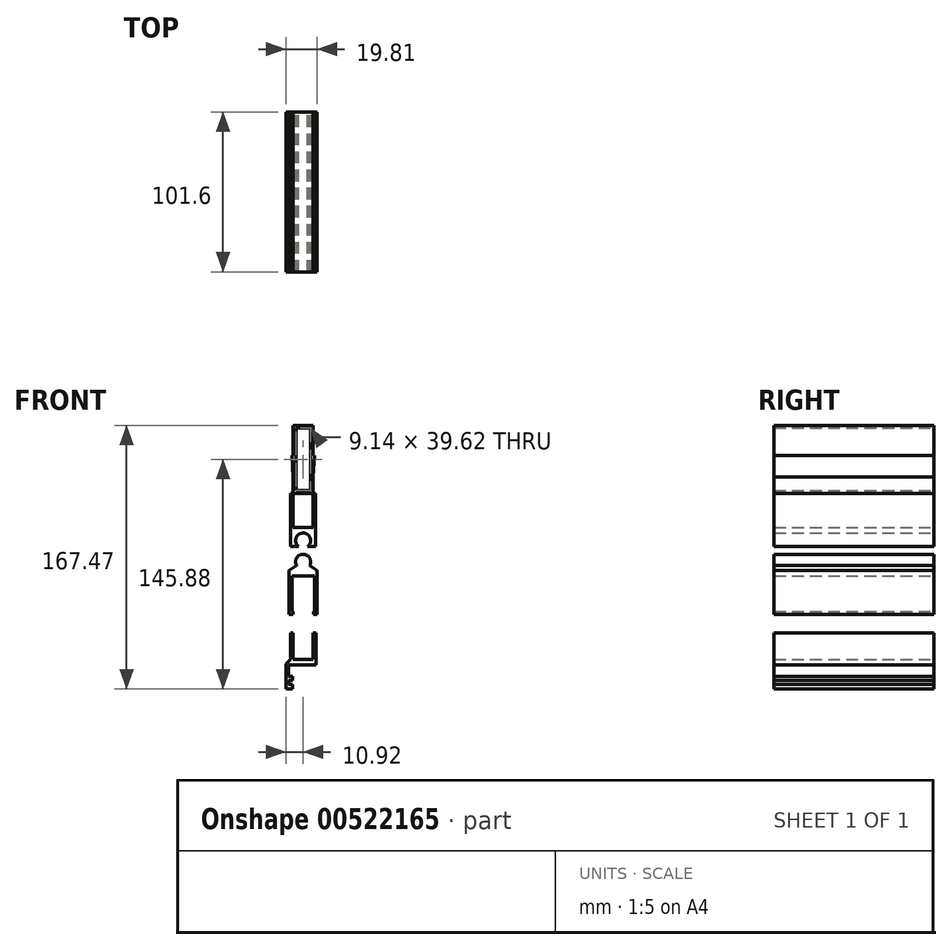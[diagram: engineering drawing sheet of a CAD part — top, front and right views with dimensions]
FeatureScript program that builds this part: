
annotation { "Feature Type Name" : "Feature", "Feature Type Description" : "" }
export const myFeature = defineFeature(function(context is Context, id is Id, definition is map)
    precondition{}
    {
        {
            var Q0;
            Q0=qCreatedBy(makeId("Front.planeOp"),FACE);
            var sketch = newSketch(context, id + "F0", { "sketchPlane" : qUnion([Q0])});
            skLineSegment(sketch, "E0", {"start": v(6.35, 0) * mm, "end": v(6.35, 10.41) * mm});
            skLineSegment(sketch, "E1", {"start": v(6.35, 10.41) * mm, "end": v(7.11, 24.13) * mm});
            skLineSegment(sketch, "E2", {"start": v(7.11, 24.13) * mm, "end": v(6.35, 24.13) * mm});
            skLineSegment(sketch, "E3", {"start": v(6.35, 24.13) * mm, "end": v(6.35, 43.18) * mm});
            skLineSegment(sketch, "E4", {"start": v(6.35, 43.18) * mm, "end": v(-0.05, 43.18) * mm});
            skLineSegment(sketch, "E5", {"start": v(6.35, 0) * mm, "end": v(0, 0) * mm});
            skLineSegment(sketch, "E6", {"start": v(0, 41.4) * mm, "end": v(4.57, 41.4) * mm});
            skLineSegment(sketch, "E7", {"start": v(4.57, 41.4) * mm, "end": v(4.57, 1.78) * mm});
            skLineSegment(sketch, "E8", {"start": v(4.57, 1.78) * mm, "end": v(0, 1.78) * mm});
            skLineSegment(sketch, "E9.MirrorCS", {"start": v(-7.11, 24.13) * mm, "end": v(-6.35, 24.13) * mm});
            skLineSegment(sketch, "E10.MirrorCS", {"start": v(-6.35, 24.13) * mm, "end": v(-6.35, 43.18) * mm});
            skLineSegment(sketch, "E11.MirrorCS", {"start": v(-6.35, 43.18) * mm, "end": v(0.05, 43.18) * mm});
            skLineSegment(sketch, "E12.MirrorCS", {"start": v(-6.35, 0) * mm, "end": v(0, 0) * mm});
            skLineSegment(sketch, "E13.MirrorCS", {"start": v(0, 41.4) * mm, "end": v(-4.57, 41.4) * mm});
            skLineSegment(sketch, "E14.MirrorCS", {"start": v(-4.57, 41.4) * mm, "end": v(-4.57, 1.78) * mm});
            skLineSegment(sketch, "E15.MirrorCS", {"start": v(-6.35, 0) * mm, "end": v(-6.35, 10.41) * mm});
            skLineSegment(sketch, "E16.MirrorCS", {"start": v(-4.57, 1.78) * mm, "end": v(0, 1.78) * mm});
            skLineSegment(sketch, "E17.MirrorCS", {"start": v(-6.35, 10.41) * mm, "end": v(-7.11, 24.13) * mm});
            skSolve(sketch);
        }
        {
            var Q0;
            Q0 = qSketchRegion(id + "F0", true);
            extrude(context, id + "F1", {"entities" : qUnion([Q0]), "depth" : 101.6 * mm, "offsetDistance" : 25.4 * mm});
        }
        {
            var Q0;
            Q0=qCreatedBy(makeId("Front.planeOp"),FACE);
            var sketch = newSketch(context, id + "F2", { "sketchPlane" : qUnion([Q0])});
            skLineSegment(sketch, "E18", {"start": v(6.35, 0) * mm, "end": v(6.35, -21.65) * mm});
            skLineSegment(sketch, "E19", {"start": v(6.35, -21.65) * mm, "end": v(-6.35, -21.65) * mm});
            skLineSegment(sketch, "E20", {"start": v(-6.35, -21.65) * mm, "end": v(-6.35, 0) * mm});
            skLineSegment(sketch, "E21", {"start": v(-6.35, 0) * mm, "end": v(-7.92, 0) * mm});
            skLineSegment(sketch, "E22", {"start": v(-7.92, 0) * mm, "end": v(-7.92, -33.78) * mm});
            skLineSegment(sketch, "E23", {"start": v(-7.92, -33.78) * mm, "end": v(-2.86, -33.78) * mm});
            skLineSegment(sketch, "E24", {"start": v(7.92, -33.78) * mm, "end": v(7.92, 0) * mm});
            skLineSegment(sketch, "E25", {"start": v(7.92, 0) * mm, "end": v(6.35, 0) * mm});
            skArc(sketch, "E26", {"start": v(2.86, -33.78) * mm, "mid": v(0, -25.2) * mm, "end": v(-2.86, -33.78) * mm});
            skPoint(sketch, "E27", {"position": v(0, -33.78) * mm});
            skLineSegment(sketch, "E28.trimOffspring", {"start": v(2.86, -33.78) * mm, "end": v(7.92, -33.78) * mm});
            skSolve(sketch);
        }
        {
            var Q0;
            Q0 = qSketchRegion(id + "F2", true);
            extrude(context, id + "F3", {"entities" : qUnion([Q0]), "depth" : 101.6 * mm, "offsetDistance" : 25.4 * mm});
        }
        {
            var Q0;
            Q0=qCreatedBy(makeId("Front.planeOp"),FACE);
            var sketch = newSketch(context, id + "F4", { "sketchPlane" : qUnion([Q0])});
            skArc(sketch, "E29", {"start": v(4.07, -45.9) * mm, "mid": v(0, -38.67) * mm, "end": v(-4.07, -45.9) * mm});
            skLineSegment(sketch, "E30", {"start": v(-4.07, -45.9) * mm, "end": v(-8.9, -48.83) * mm});
            skLineSegment(sketch, "E31", {"start": v(4.07, -45.9) * mm, "end": v(8.9, -48.83) * mm});
            skLineSegment(sketch, "E32", {"start": v(-8.9, -48.83) * mm, "end": v(-8.89, -76.77) * mm});
            skLineSegment(sketch, "E33", {"start": v(-8.89, -76.77) * mm, "end": v(-6.55, -76.77) * mm});
            skLineSegment(sketch, "E34", {"start": v(-6.55, -76.77) * mm, "end": v(-6.55, -74.99) * mm});
            skLineSegment(sketch, "E35", {"start": v(-6.55, -74.99) * mm, "end": v(-7.11, -74.99) * mm});
            skLineSegment(sketch, "E36", {"start": v(-7.11, -74.99) * mm, "end": v(-7.11, -52.38) * mm});
            skLineSegment(sketch, "E37", {"start": v(-7.11, -52.38) * mm, "end": v(7.11, -52.38) * mm});
            skLineSegment(sketch, "E38", {"start": v(7.11, -52.38) * mm, "end": v(7.11, -74.99) * mm});
            skLineSegment(sketch, "E39", {"start": v(7.11, -74.99) * mm, "end": v(6.55, -74.99) * mm});
            skLineSegment(sketch, "E40", {"start": v(6.55, -74.99) * mm, "end": v(6.55, -76.77) * mm});
            skLineSegment(sketch, "E41", {"start": v(6.55, -76.77) * mm, "end": v(8.89, -76.77) * mm});
            skLineSegment(sketch, "E42", {"start": v(8.89, -76.77) * mm, "end": v(8.9, -48.83) * mm});
            skSolve(sketch);
        }
        {
            var Q0;
            Q0 = qSketchRegion(id + "F4", true);
            extrude(context, id + "F5", {"entities" : qUnion([Q0]), "depth" : 101.6 * mm, "offsetDistance" : 25.4 * mm});
        }
        {
            var Q0;
            Q0=qCreatedBy(makeId("Front.planeOp"),FACE);
            var sketch = newSketch(context, id + "F6", { "sketchPlane" : qUnion([Q0])});
            skLineSegment(sketch, "E43", {"start": v(-6.35, -88.73) * mm, "end": v(-6.35, -105.5) * mm});
            skLineSegment(sketch, "E44", {"start": v(-6.35, -105.5) * mm, "end": v(6.35, -105.5) * mm});
            skLineSegment(sketch, "E45", {"start": v(6.35, -105.5) * mm, "end": v(6.35, -88.73) * mm});
            skLineSegment(sketch, "E46", {"start": v(6.35, -88.73) * mm, "end": v(8.13, -88.73) * mm});
            skLineSegment(sketch, "E47", {"start": v(8.13, -88.73) * mm, "end": v(8.13, -109.05) * mm});
            skLineSegment(sketch, "E48", {"start": v(8.13, -109.05) * mm, "end": v(-9.14, -109.05) * mm});
            skLineSegment(sketch, "E49", {"start": v(-9.14, -109.05) * mm, "end": v(-9.14, -116.17) * mm});
            skLineSegment(sketch, "E50", {"start": v(-9.14, -116.17) * mm, "end": v(-6.86, -116.17) * mm});
            skLineSegment(sketch, "E51", {"start": v(-6.86, -116.17) * mm, "end": v(-6.86, -118.96) * mm});
            skLineSegment(sketch, "E52", {"start": v(-6.86, -118.96) * mm, "end": v(-9.14, -118.96) * mm});
            skLineSegment(sketch, "E53", {"start": v(-9.14, -118.96) * mm, "end": v(-9.14, -121.5) * mm});
            skLineSegment(sketch, "E54", {"start": v(-9.14, -121.5) * mm, "end": v(-6.86, -121.5) * mm});
            skLineSegment(sketch, "E55", {"start": v(-6.86, -121.5) * mm, "end": v(-6.86, -124.3) * mm});
            skLineSegment(sketch, "E56", {"start": v(-6.86, -124.3) * mm, "end": v(-10.92, -124.3) * mm});
            skLineSegment(sketch, "E57", {"start": v(-10.92, -124.3) * mm, "end": v(-10.92, -108.3) * mm});
            skLineSegment(sketch, "E58", {"start": v(-10.92, -108.3) * mm, "end": v(-8.13, -105.5) * mm});
            skLineSegment(sketch, "E59", {"start": v(-8.13, -105.5) * mm, "end": v(-8.13, -88.73) * mm});
            skLineSegment(sketch, "E60", {"start": v(-8.13, -88.73) * mm, "end": v(-6.35, -88.73) * mm});
            skSolve(sketch);
        }
        {
            var Q0;
            Q0 = qSketchRegion(id + "F6", true);
            extrude(context, id + "F7", {"entities" : qUnion([Q0]), "depth" : 101.6 * mm, "offsetDistance" : 25.4 * mm});
        }
    });
